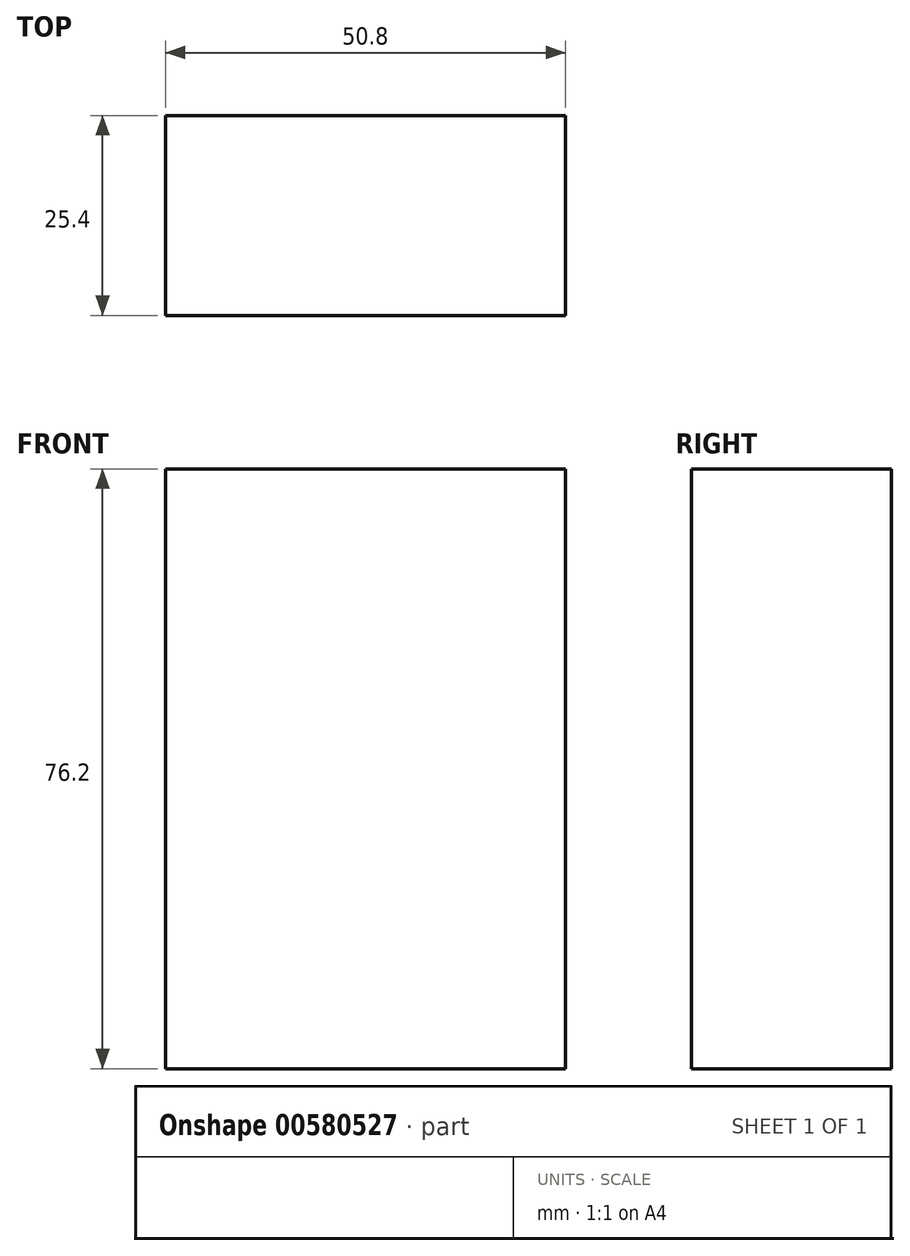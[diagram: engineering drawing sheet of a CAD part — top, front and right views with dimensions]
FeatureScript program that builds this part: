
annotation { "Feature Type Name" : "Feature", "Feature Type Description" : "" }
export const myFeature = defineFeature(function(context is Context, id is Id, definition is map)
    precondition{}
    {
        {
            var Q0;
            Q0=qCreatedBy(makeId("Front.planeOp"),FACE);
            var sketch = newSketch(context, id + "F0", { "sketchPlane" : qUnion([Q0])});
            skLineSegment(sketch, "E0.bottom", {"start": v(0, 0) * mm, "end": v(-50.8, 0) * mm});
            skLineSegment(sketch, "E0.top", {"start": v(0, 76.2) * mm, "end": v(-50.8, 76.2) * mm});
            skLineSegment(sketch, "E0.left", {"start": v(0, 0) * mm, "end": v(0, 76.2) * mm});
            skLineSegment(sketch, "E0.right", {"start": v(-50.8, 0) * mm, "end": v(-50.8, 76.2) * mm});
            skSolve(sketch);
        }
        {
            var Q0;
            Q0 = qSketchRegion(id + "F0", true);
            extrude(context, id + "F1", {"entities" : qUnion([Q0]), "depth" : 25.4 * mm, "offsetDistance" : 25.4 * mm});
        }
    });
